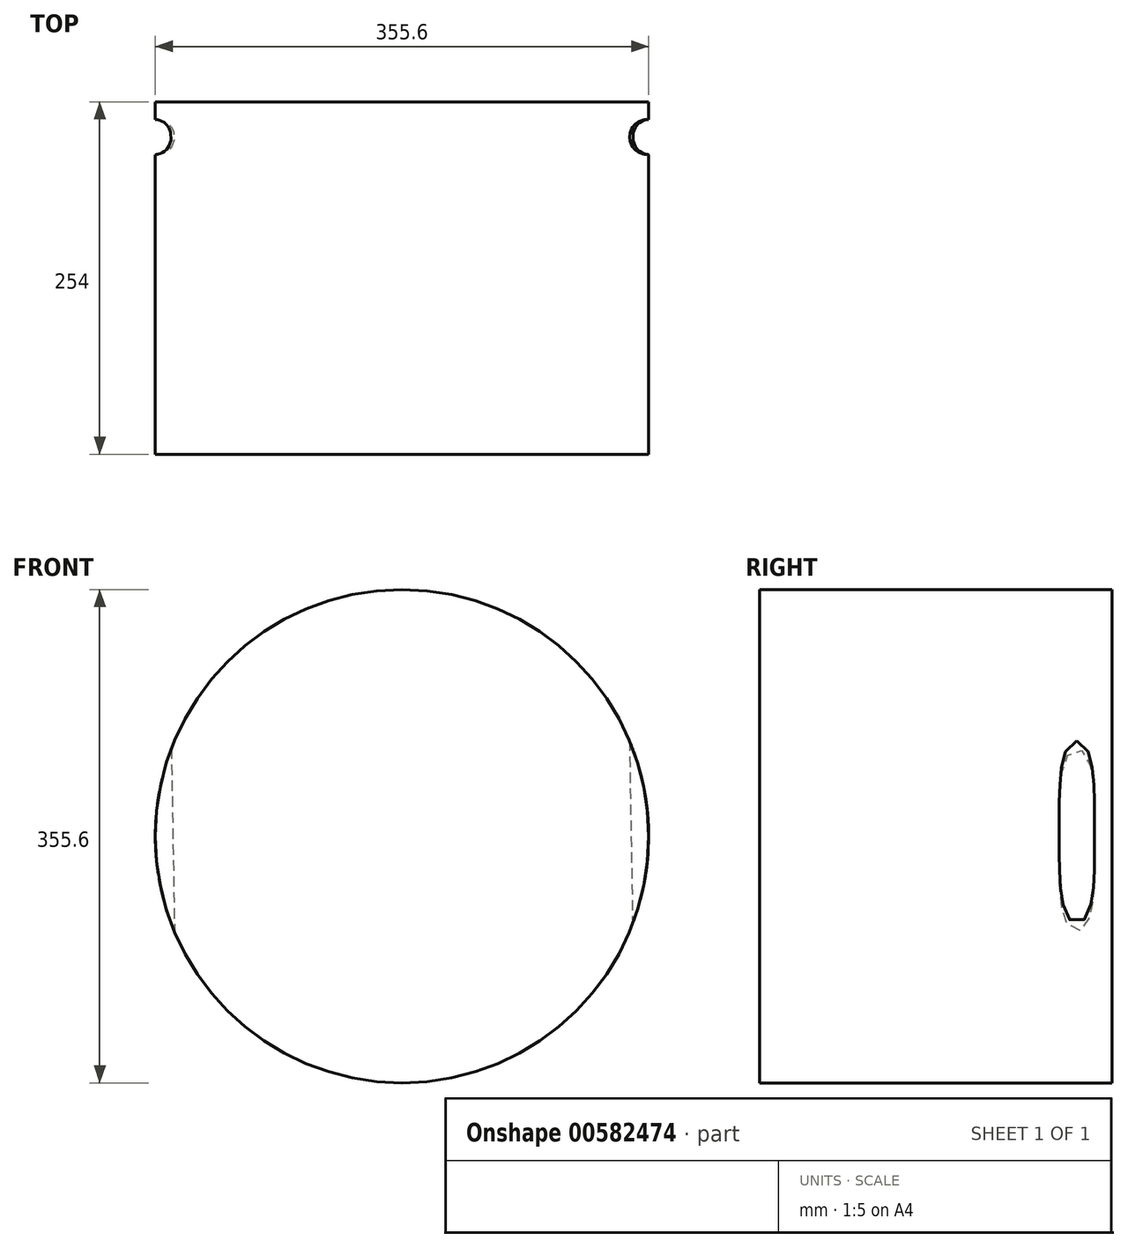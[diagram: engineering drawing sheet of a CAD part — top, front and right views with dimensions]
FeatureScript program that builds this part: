
annotation { "Feature Type Name" : "Feature", "Feature Type Description" : "" }
export const myFeature = defineFeature(function(context is Context, id is Id, definition is map)
    precondition{}
    {
        {
            var Q0;
            Q0=qCreatedBy(makeId("Front.planeOp"),FACE);
            var sketch = newSketch(context, id + "F0", { "sketchPlane" : qUnion([Q0])});
            skCircle(sketch, "E0", {"center": v(0, 0) * mm, "radius": 177.8 * mm});
            skSolve(sketch);
        }
        {
            var Q0;
            Q0 = qSketchRegion(id + "F0", false);
            extrude(context, id + "F1", {"entities" : qUnion([Q0]), "depth" : 254 * mm});
        }
        {
            var Q0;
            Q0=qCreatedBy(makeId("Top.planeOp"),FACE);
            var sketch = newSketch(context, id + "F2", { "sketchPlane" : qUnion([Q0])});
            skLineSegment(sketch, "E1", {"start": v(0, -254) * mm, "end": v(0, 0) * mm});
            skSolve(sketch);
        }
        {
            var Q0;
            Q0=sQuery(id+"F2.wireOp",EDGE,"E1");
            cPlane(context, id + "F3", {"entities" : qUnion([Q0]), "cplaneType" : CPlaneType.LINE_ANGLE, "offset" : 25.4 * mm, "angle" : 1 * degree, "oppositeDirection" : true, "width" : 152.4 * mm, "height" : 152.4 * mm});
        }
        {
            var Q0;
            Q0=qCreatedBy(id+"F3.planeOp",FACE);
            var sketch = newSketch(context, id + "F4", { "sketchPlane" : qUnion([Q0])});
            skLineSegment(sketch, "E2", {"start": v(177.8, -254) * mm, "end": v(177.8, 0) * mm});
            skLineSegment(sketch, "E3", {"start": v(177.8, 0) * mm, "end": v(177.8, -254) * mm});
            skCircle(sketch, "E4", {"center": v(177.8, -25.4) * mm, "radius": 12.7 * mm});
            skCircle(sketch, "E5", {"center": v(-177.8, -25.4) * mm, "radius": 12.7 * mm});
            skSolve(sketch);
        }
        {
            var Q0;
            Q0 = qSketchRegion(id + "F4", false);
            extrude(context, id + "F5", {"entities" : qUnion([Q0]), "operationType" : NewBodyOperationType.REMOVE, "endBound" : BoundingType.SYMMETRIC, "depth" : 355.6 * mm});
        }
    });
